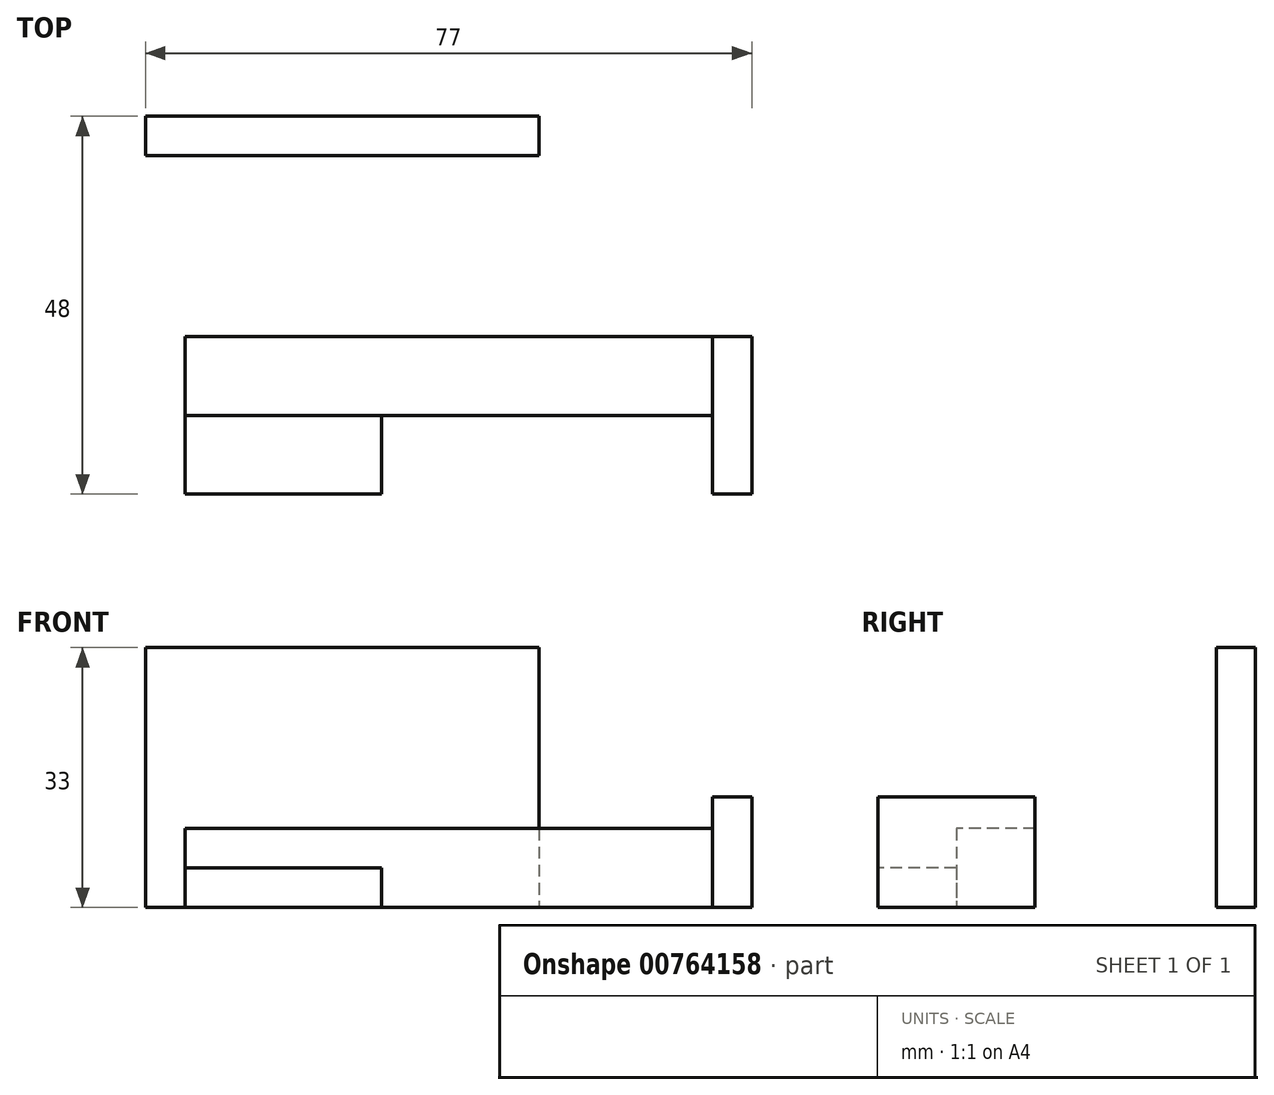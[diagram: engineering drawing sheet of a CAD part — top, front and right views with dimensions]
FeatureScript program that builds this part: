
annotation { "Feature Type Name" : "Feature", "Feature Type Description" : "" }
export const myFeature = defineFeature(function(context is Context, id is Id, definition is map)
    precondition{}
    {
        {
            var Q0;
            Q0=qCreatedBy(makeId("Top.planeOp"),FACE);
            var sketch = newSketch(context, id + "F0", { "sketchPlane" : qUnion([Q0])});
            skLineSegment(sketch, "E0.bottom", {"start": v(-38.5, 24) * mm, "end": v(38.5, 24) * mm});
            skLineSegment(sketch, "E0.top", {"start": v(-38.5, -24) * mm, "end": v(-8.5, -24) * mm});
            skLineSegment(sketch, "E0.left", {"start": v(-38.5, 24) * mm, "end": v(-38.5, -24) * mm});
            skLineSegment(sketch, "E0.right", {"start": v(38.5, 24) * mm, "end": v(38.5, -24) * mm});
            skPoint(sketch, "E0.middle", {"position": v(0, 0) * mm});
            skLineSegment(sketch, "E1", {"start": v(-33.5, 19) * mm, "end": v(-33.5, -24) * mm});
            skLineSegment(sketch, "E2", {"start": v(-38.5, 19) * mm, "end": v(11.5, 19) * mm});
            skPoint(sketch, "E3.orphan", {"position": v(-33.5, 24) * mm});
            skLineSegment(sketch, "E4", {"start": v(-8.5, 19) * mm, "end": v(-8.5, -4) * mm});
            skLineSegment(sketch, "E5", {"start": v(-33.5, -14) * mm, "end": v(33.5, -14) * mm});
            skLineSegment(sketch, "E6", {"start": v(33.5, -24) * mm, "end": v(33.5, 24) * mm});
            skLineSegment(sketch, "E7.trimOffspring", {"start": v(33.5, -24) * mm, "end": v(38.5, -24) * mm});
            skPoint(sketch, "E8.orphan", {"position": v(-38.5, -14) * mm});
            skLineSegment(sketch, "E9", {"start": v(-33.5, -4) * mm, "end": v(33.5, -4) * mm});
            skLineSegment(sketch, "E10.trimOffspring", {"start": v(-8.5, -14) * mm, "end": v(-8.5, -24) * mm});
            skLineSegment(sketch, "E11", {"start": v(-33.5, 19) * mm, "end": v(-8.5, -4) * mm});
            skLineSegment(sketch, "E12", {"start": v(1.5, 19) * mm, "end": v(1.5, -4) * mm});
            skLineSegment(sketch, "E13", {"start": v(11.5, 19) * mm, "end": v(11.5, -4) * mm});
            skLineSegment(sketch, "E14", {"start": v(11.5, 19) * mm, "end": v(11.5, 24) * mm});
            skLineSegment(sketch, "E15", {"start": v(33.5, -4) * mm, "end": v(38.5, -4) * mm});
            skSolve(sketch);
        }
        {
            var Q0;
            {var subQ0=sQuery(id+"F0.wireOp",EDGE,"E10.trimOffspring");Q0=makeQuery(id+"F0.imprint","IMPRINT",FACE,{"disambiguationData":[TD([[makeQuery(id+"F0.imprint","IMPRINT",EDGE,{"derivedFrom":subQ0}),-1.0]])]});}
            extrude(context, id + "F1", {"entities" : qUnion([Q0]), "depth" : 5 * mm, "offsetDistance" : 25 * mm});
        }
        {
            var Q0;
            {var subQ1=sQuery(id+"F0.wireOp",EDGE,"E5");var subQ4=sQuery(id+"F0.wireOp",EDGE,"E1");var subQ5=makeQuery(id+"F0.imprint","INTERSECT",VERTEX,{"derivedFrom":[subQ4,subQ1]});Q0=makeQuery(id+"F0.imprint","IMPRINT",FACE,{"disambiguationData":[TD([[makeQuery(id+"F0.imprint","IMPRINT",EDGE,{"disambiguationData":[TD([[subQ5,1.0]])],"derivedFrom":subQ4}),1.0]])]});}
            extrude(context, id + "F2", {"entities" : qUnion([Q0]), "operationType" : NewBodyOperationType.ADD, "depth" : 10 * mm, "offsetDistance" : 25 * mm});
        }
        {
            var Q0;
            {var subQ0=sQuery(id+"F0.wireOp",EDGE,"E7.trimOffspring");Q0=makeQuery(id+"F0.imprint","IMPRINT",FACE,{"disambiguationData":[TD([[makeQuery(id+"F0.imprint","IMPRINT",EDGE,{"derivedFrom":subQ0}),1.0]])]});}
            extrude(context, id + "F3", {"entities" : qUnion([Q0]), "operationType" : NewBodyOperationType.ADD, "depth" : 14 * mm, "offsetDistance" : 25 * mm});
        }
        {
            var Q0;
            {var subQ7=sQuery(id+"F0.wireOp",EDGE,"E14");Q0=makeQuery(id+"F0.imprint","IMPRINT",FACE,{"disambiguationData":[TD([[makeQuery(id+"F0.imprint","IMPRINT",EDGE,{"derivedFrom":subQ7}),1.0]])]});}
            extrude(context, id + "F4", {"entities" : qUnion([Q0]), "depth" : 33 * mm, "offsetDistance" : 25 * mm});
        }
    });
